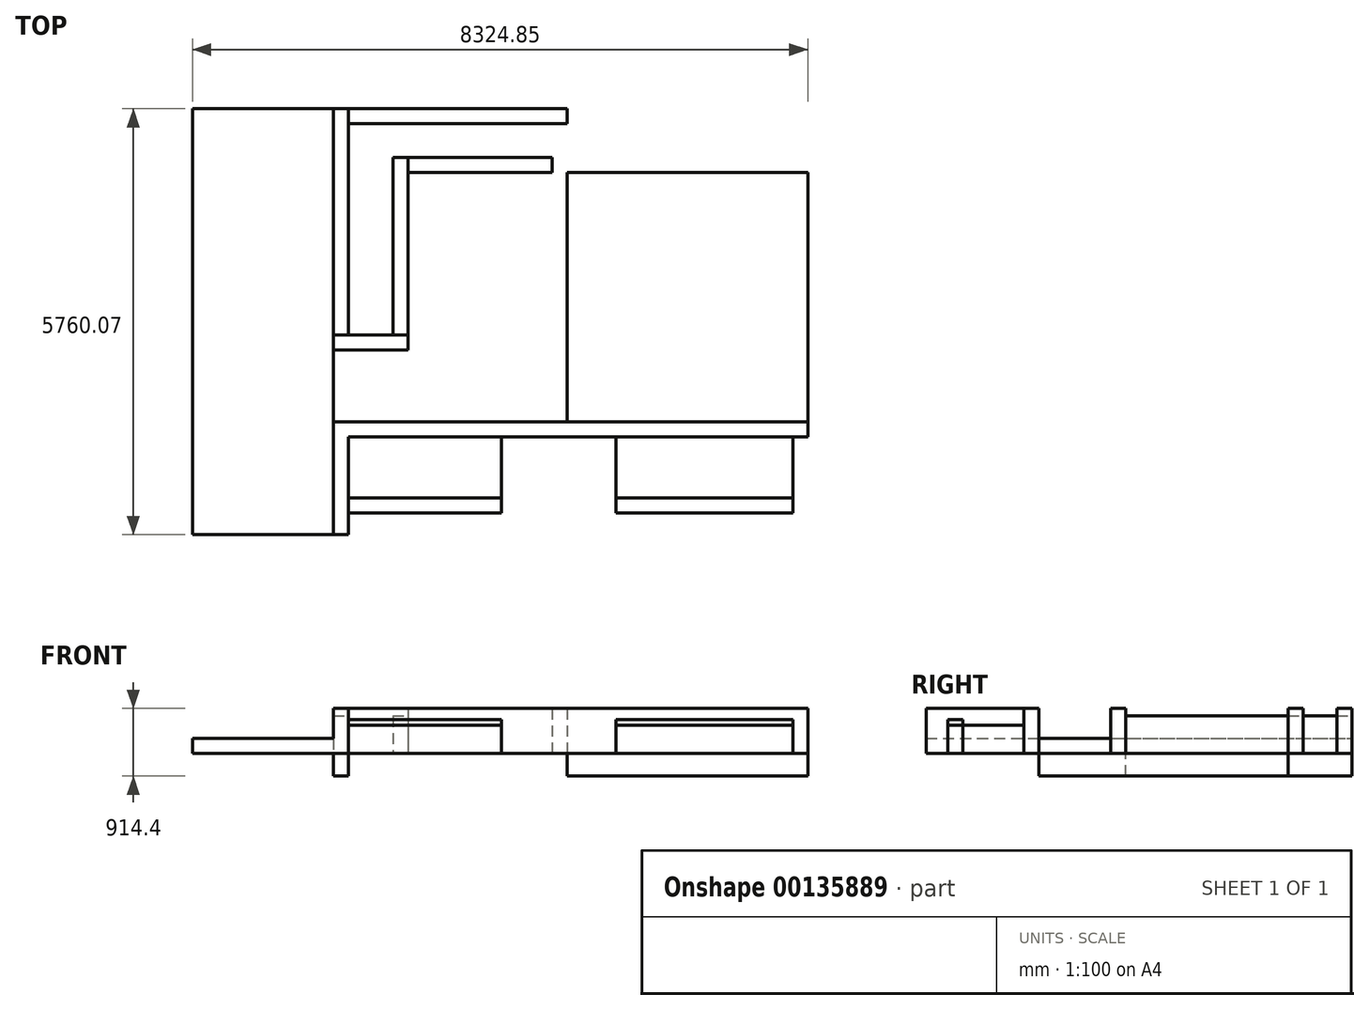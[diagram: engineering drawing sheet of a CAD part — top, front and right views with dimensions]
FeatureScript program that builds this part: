
annotation { "Feature Type Name" : "Feature", "Feature Type Description" : "" }
export const myFeature = defineFeature(function(context is Context, id is Id, definition is map)
    precondition{}
    {
        {
            var Q0;
            Q0=qCreatedBy(makeId("Top.planeOp"),FACE);
            var sketch = newSketch(context, id + "F0", { "sketchPlane" : qUnion([Q0])});
            skLineSegment(sketch, "E0.bottom", {"start": v(0, 0) * mm, "end": v(1905, 0) * mm});
            skLineSegment(sketch, "E0.top", {"start": v(0, 5760.07) * mm, "end": v(1905, 5760.07) * mm});
            skLineSegment(sketch, "E0.left", {"start": v(0, 0) * mm, "end": v(0, 5760.07) * mm});
            skLineSegment(sketch, "E0.right", {"start": v(1905, 0) * mm, "end": v(1905, 5760.07) * mm});
            skLineSegment(sketch, "E1.bottom", {"start": v(1905, 0) * mm, "end": v(2108.2, 0) * mm});
            skLineSegment(sketch, "E1.top", {"start": v(1905, 1320.8) * mm, "end": v(2108.2, 1320.8) * mm});
            skLineSegment(sketch, "E1.left", {"start": v(1905, 0) * mm, "end": v(1905, 1320.8) * mm});
            skLineSegment(sketch, "E1.right", {"start": v(2108.2, 0) * mm, "end": v(2108.2, 1320.8) * mm});
            skLineSegment(sketch, "E2.bottom", {"start": v(1905, 1320.8) * mm, "end": v(8324.85, 1320.8) * mm});
            skLineSegment(sketch, "E2.top", {"start": v(1905, 1524) * mm, "end": v(8324.85, 1524) * mm});
            skLineSegment(sketch, "E2.left", {"start": v(1905, 1320.8) * mm, "end": v(1905, 1524) * mm});
            skLineSegment(sketch, "E2.right", {"start": v(8324.85, 1320.8) * mm, "end": v(8324.85, 1524) * mm});
            skLineSegment(sketch, "E3.bottom", {"start": v(1905, 2496.17) * mm, "end": v(2914.65, 2496.17) * mm});
            skLineSegment(sketch, "E3.top", {"start": v(1905, 2699.37) * mm, "end": v(2914.65, 2699.37) * mm});
            skLineSegment(sketch, "E3.left", {"start": v(1905, 2496.17) * mm, "end": v(1905, 2699.37) * mm});
            skLineSegment(sketch, "E3.right", {"start": v(2914.65, 2496.17) * mm, "end": v(2914.65, 2699.37) * mm});
            skLineSegment(sketch, "E4.bottom", {"start": v(1905, 2699.37) * mm, "end": v(2108.2, 2699.37) * mm});
            skLineSegment(sketch, "E4.top", {"start": v(1905, 5760.07) * mm, "end": v(2108.2, 5760.07) * mm});
            skLineSegment(sketch, "E4.left", {"start": v(1905, 2699.37) * mm, "end": v(1905, 5760.07) * mm});
            skLineSegment(sketch, "E4.right", {"start": v(2108.2, 2699.37) * mm, "end": v(2108.2, 5760.07) * mm});
            skLineSegment(sketch, "E5.bottom", {"start": v(2108.2, 5760.07) * mm, "end": v(5067.3, 5760.07) * mm});
            skLineSegment(sketch, "E5.top", {"start": v(2108.2, 5556.87) * mm, "end": v(5067.3, 5556.87) * mm});
            skLineSegment(sketch, "E5.left", {"start": v(2108.2, 5760.07) * mm, "end": v(2108.2, 5556.87) * mm});
            skLineSegment(sketch, "E5.right", {"start": v(5067.3, 5760.07) * mm, "end": v(5067.3, 5556.87) * mm});
            skLineSegment(sketch, "E6.bottom", {"start": v(5067.3, 5556.87) * mm, "end": v(4864.1, 5556.87) * mm});
            skLineSegment(sketch, "E6.top", {"start": v(5067.3, 4896.47) * mm, "end": v(4864.1, 4896.47) * mm});
            skLineSegment(sketch, "E6.left", {"start": v(5067.3, 5556.87) * mm, "end": v(5067.3, 4896.47) * mm});
            skLineSegment(sketch, "E6.right", {"start": v(4864.1, 5556.87) * mm, "end": v(4864.1, 4896.47) * mm});
            skPoint(sketch, "E7.oppositeSnap0", {"position": v(2914.65, 2597.77) * mm});
            skLineSegment(sketch, "E7.bottom", {"start": v(4864.1, 4896.47) * mm, "end": v(2914.65, 4896.47) * mm});
            skLineSegment(sketch, "E7.top", {"start": v(4864.1, 5099.67) * mm, "end": v(2914.65, 5099.67) * mm});
            skLineSegment(sketch, "E7.left", {"start": v(4864.1, 4896.47) * mm, "end": v(4864.1, 5099.67) * mm});
            skLineSegment(sketch, "E7.right", {"start": v(2914.65, 4896.47) * mm, "end": v(2914.65, 5099.67) * mm});
            skLineSegment(sketch, "E8.bottom", {"start": v(2914.65, 2699.37) * mm, "end": v(2711.45, 2699.37) * mm});
            skLineSegment(sketch, "E8.top", {"start": v(2914.65, 5099.67) * mm, "end": v(2711.45, 5099.67) * mm});
            skLineSegment(sketch, "E8.left", {"start": v(2914.65, 2699.37) * mm, "end": v(2914.65, 5099.67) * mm});
            skLineSegment(sketch, "E8.right", {"start": v(2711.45, 2699.37) * mm, "end": v(2711.45, 5099.67) * mm});
            skLineSegment(sketch, "E9.bottom", {"start": v(5067.3, 4896.47) * mm, "end": v(8324.85, 4896.47) * mm});
            skLineSegment(sketch, "E9.top", {"start": v(5067.3, 1524) * mm, "end": v(8324.85, 1524) * mm});
            skLineSegment(sketch, "E9.left", {"start": v(5067.3, 4896.47) * mm, "end": v(5067.3, 1524) * mm});
            skLineSegment(sketch, "E9.right", {"start": v(8324.85, 4896.47) * mm, "end": v(8324.85, 1524) * mm});
            skLineSegment(sketch, "E10.bottom", {"start": v(4381.5, 1320.8) * mm, "end": v(4178.3, 1320.8) * mm});
            skLineSegment(sketch, "E10.top", {"start": v(4381.5, 292.1) * mm, "end": v(4178.3, 292.1) * mm});
            skLineSegment(sketch, "E10.left", {"start": v(4381.5, 1320.8) * mm, "end": v(4381.5, 292.1) * mm});
            skLineSegment(sketch, "E10.right", {"start": v(4178.3, 1320.8) * mm, "end": v(4178.3, 292.1) * mm});
            skLineSegment(sketch, "E11.bottom", {"start": v(4178.3, 292.1) * mm, "end": v(2108.2, 292.1) * mm});
            skLineSegment(sketch, "E11.top", {"start": v(4178.3, 495.3) * mm, "end": v(2108.2, 495.3) * mm});
            skLineSegment(sketch, "E11.left", {"start": v(4178.3, 292.1) * mm, "end": v(4178.3, 495.3) * mm});
            skLineSegment(sketch, "E11.right", {"start": v(2108.2, 292.1) * mm, "end": v(2108.2, 495.3) * mm});
            skLineSegment(sketch, "E12.bottom", {"start": v(8324.85, 1320.8) * mm, "end": v(8121.65, 1320.8) * mm});
            skLineSegment(sketch, "E12.top", {"start": v(8324.85, -203.2) * mm, "end": v(8121.65, -203.2) * mm});
            skLineSegment(sketch, "E12.left", {"start": v(8324.85, 1320.8) * mm, "end": v(8324.85, -203.2) * mm});
            skLineSegment(sketch, "E12.right", {"start": v(8121.65, 1320.8) * mm, "end": v(8121.65, -203.2) * mm});
            skLineSegment(sketch, "E13.bottom", {"start": v(5527.25, 1320.8) * mm, "end": v(5730.45, 1320.8) * mm});
            skLineSegment(sketch, "E13.top", {"start": v(5527.25, 292.1) * mm, "end": v(5730.45, 292.1) * mm});
            skLineSegment(sketch, "E13.left", {"start": v(5527.25, 1320.8) * mm, "end": v(5527.25, 292.1) * mm});
            skLineSegment(sketch, "E13.right", {"start": v(5730.45, 1320.8) * mm, "end": v(5730.45, 292.1) * mm});
            skLineSegment(sketch, "E14.bottom", {"start": v(5730.45, 292.1) * mm, "end": v(8121.65, 292.1) * mm});
            skLineSegment(sketch, "E14.top", {"start": v(5730.45, 495.3) * mm, "end": v(8121.65, 495.3) * mm});
            skLineSegment(sketch, "E14.left", {"start": v(5730.45, 292.1) * mm, "end": v(5730.45, 495.3) * mm});
            skLineSegment(sketch, "E14.right", {"start": v(8121.65, 292.1) * mm, "end": v(8121.65, 495.3) * mm});
            skSolve(sketch);
        }
        {
            var Q0;
            Q0=makeQuery(id+"F0.imprint","IMPRINT",FACE,{"disambiguationData":[TD([[makeQuery(id+"F0.imprint","IMPRINT",EDGE,{"derivedFrom":sQuery(id+"F0.wireOp",EDGE,"E0.bottom")}),1.0]])]});
            extrude(context, id + "F1", {"entities" : qUnion([Q0]), "depth" : 203.2 * mm});
        }
        {
            var Q0;
            Q0=makeQuery(id+"F0.imprint","IMPRINT",FACE,{"disambiguationData":[TD([[makeQuery(id+"F0.imprint","IMPRINT",EDGE,{"derivedFrom":sQuery(id+"F0.wireOp",EDGE,"E4.bottom")}),1.0]])]});
            var Q1;
            Q1=makeQuery(id+"F0.imprint","IMPRINT",FACE,{"disambiguationData":[TD([[makeQuery(id+"F0.imprint","IMPRINT",EDGE,{"derivedFrom":sQuery(id+"F0.wireOp",EDGE,"E5.bottom")}),-1.0]])]});
            var Q2;
            {var subQ3=sQuery(id+"F0.wireOp",EDGE,"E8.bottom");Q2=makeQuery(id+"F0.imprint","IMPRINT",FACE,{"disambiguationData":[TD([[makeQuery(id+"F0.imprint","IMPRINT",EDGE,{"derivedFrom":subQ3}),-1.0]])]});}
            var Q3;
            {var subQ0=sQuery(id+"F0.wireOp",EDGE,"E7.bottom");Q3=makeQuery(id+"F0.imprint","IMPRINT",FACE,{"disambiguationData":[TD([[makeQuery(id+"F0.imprint","IMPRINT",EDGE,{"derivedFrom":subQ0}),-1.0]])]});}
            var Q4;
            Q4=makeQuery(id+"F0.imprint","IMPRINT",FACE,{"disambiguationData":[TD([[makeQuery(id+"F0.imprint","IMPRINT",EDGE,{"derivedFrom":sQuery(id+"F0.wireOp",EDGE,"E6.bottom")}),1.0]])]});
            var Q5;
            Q5=makeQuery(id+"F0.imprint","IMPRINT",FACE,{"disambiguationData":[TD([[makeQuery(id+"F0.imprint","IMPRINT",EDGE,{"derivedFrom":sQuery(id+"F0.wireOp",EDGE,"E3.bottom")}),1.0]])]});
            var Q6;
            {var subQ4=sQuery(id+"F0.wireOp",EDGE,"E1.bottom");Q6=makeQuery(id+"F0.imprint","IMPRINT",FACE,{"disambiguationData":[TD([[makeQuery(id+"F0.imprint","IMPRINT",EDGE,{"derivedFrom":subQ4}),1.0]])]});}
            var Q7;
            Q7=makeQuery(id+"F0.imprint","IMPRINT",FACE,{"disambiguationData":[TD([[makeQuery(id+"F0.imprint","IMPRINT",EDGE,{"derivedFrom":sQuery(id+"F0.wireOp",EDGE,"E2.top")}),-1.0]])]});
            var Q8;
            {var subQ1=sQuery(id+"F0.wireOp",EDGE,"E12.bottom");Q8=makeQuery(id+"F0.imprint","IMPRINT",FACE,{"disambiguationData":[TD([[makeQuery(id+"F0.imprint","IMPRINT",EDGE,{"derivedFrom":subQ1}),1.0]])]});}
            extrude(context, id + "F2", {"entities" : qUnion([Q0, Q1, Q2, Q3, Q4, Q5, Q6, Q7, Q8]), "operationType" : NewBodyOperationType.ADD, "depth" : 609.6 * mm});
        }
        {
            var Q0;
            Q0=makeQuery(id+"F0.imprint","IMPRINT",FACE,{"disambiguationData":[TD([[makeQuery(id+"F0.imprint","IMPRINT",EDGE,{"derivedFrom":sQuery(id+"F0.wireOp",EDGE,"E10.bottom")}),1.0]])]});
            var Q1;
            Q1=makeQuery(id+"F0.imprint","IMPRINT",FACE,{"disambiguationData":[TD([[makeQuery(id+"F0.imprint","IMPRINT",EDGE,{"derivedFrom":sQuery(id+"F0.wireOp",EDGE,"E11.bottom")}),-1.0]])]});
            var Q2;
            Q2=makeQuery(id+"F0.imprint","IMPRINT",FACE,{"disambiguationData":[TD([[makeQuery(id+"F0.imprint","IMPRINT",EDGE,{"derivedFrom":sQuery(id+"F0.wireOp",EDGE,"E13.bottom")}),-1.0]])]});
            var Q3;
            Q3=makeQuery(id+"F0.imprint","IMPRINT",FACE,{"disambiguationData":[TD([[makeQuery(id+"F0.imprint","IMPRINT",EDGE,{"derivedFrom":sQuery(id+"F0.wireOp",EDGE,"E14.bottom")}),1.0]])]});
            extrude(context, id + "F3", {"entities" : qUnion([Q0, Q1, Q2, Q3]), "operationType" : NewBodyOperationType.ADD, "depth" : 457.2 * mm});
        }
        {
            var Q0;
            Q0=makeQuery(id+"F0.imprint","IMPRINT",FACE,{"disambiguationData":[TD([[makeQuery(id+"F0.imprint","IMPRINT",EDGE,{"derivedFrom":sQuery(id+"F0.wireOp",EDGE,"E0.right")}),-1.0]])]});
            var Q1;
            Q1=makeQuery(id+"F0.imprint","IMPRINT",FACE,{"disambiguationData":[TD([[makeQuery(id+"F0.imprint","IMPRINT",EDGE,{"derivedFrom":sQuery(id+"F0.wireOp",EDGE,"E9.bottom")}),-1.0]])]});
            extrude(context, id + "F4", {"entities" : qUnion([Q0, Q1]), "oppositeDirection" : true, "depth" : 304.8 * mm});
        }
        {
            var Q0;
            Q0=makeQuery(id+"F0.imprint","IMPRINT",FACE,{"disambiguationData":[TD([[makeQuery(id+"F0.imprint","IMPRINT",EDGE,{"derivedFrom":sQuery(id+"F0.wireOp",EDGE,"E3.top")}),1.0]])]});
            extrude(context, id + "F5", {"entities" : qUnion([Q0]), "depth" : 508 * mm});
        }
        {
            var Q0;
            {var subQ4=sQuery(id+"F0.wireOp",EDGE,"E10.right");Q0=makeQuery(id+"F0.imprint","IMPRINT",FACE,{"disambiguationData":[TD([[makeQuery(id+"F0.imprint","IMPRINT",EDGE,{"derivedFrom":subQ4}),-1.0]])]});}
            var Q1;
            {var subQ3=sQuery(id+"F0.wireOp",EDGE,"E13.right");Q1=makeQuery(id+"F0.imprint","IMPRINT",FACE,{"disambiguationData":[TD([[makeQuery(id+"F0.imprint","IMPRINT",EDGE,{"derivedFrom":subQ3}),1.0]])]});}
            extrude(context, id + "F6", {"entities" : qUnion([Q0, Q1]), "depth" : 381 * mm});
        }
    });
